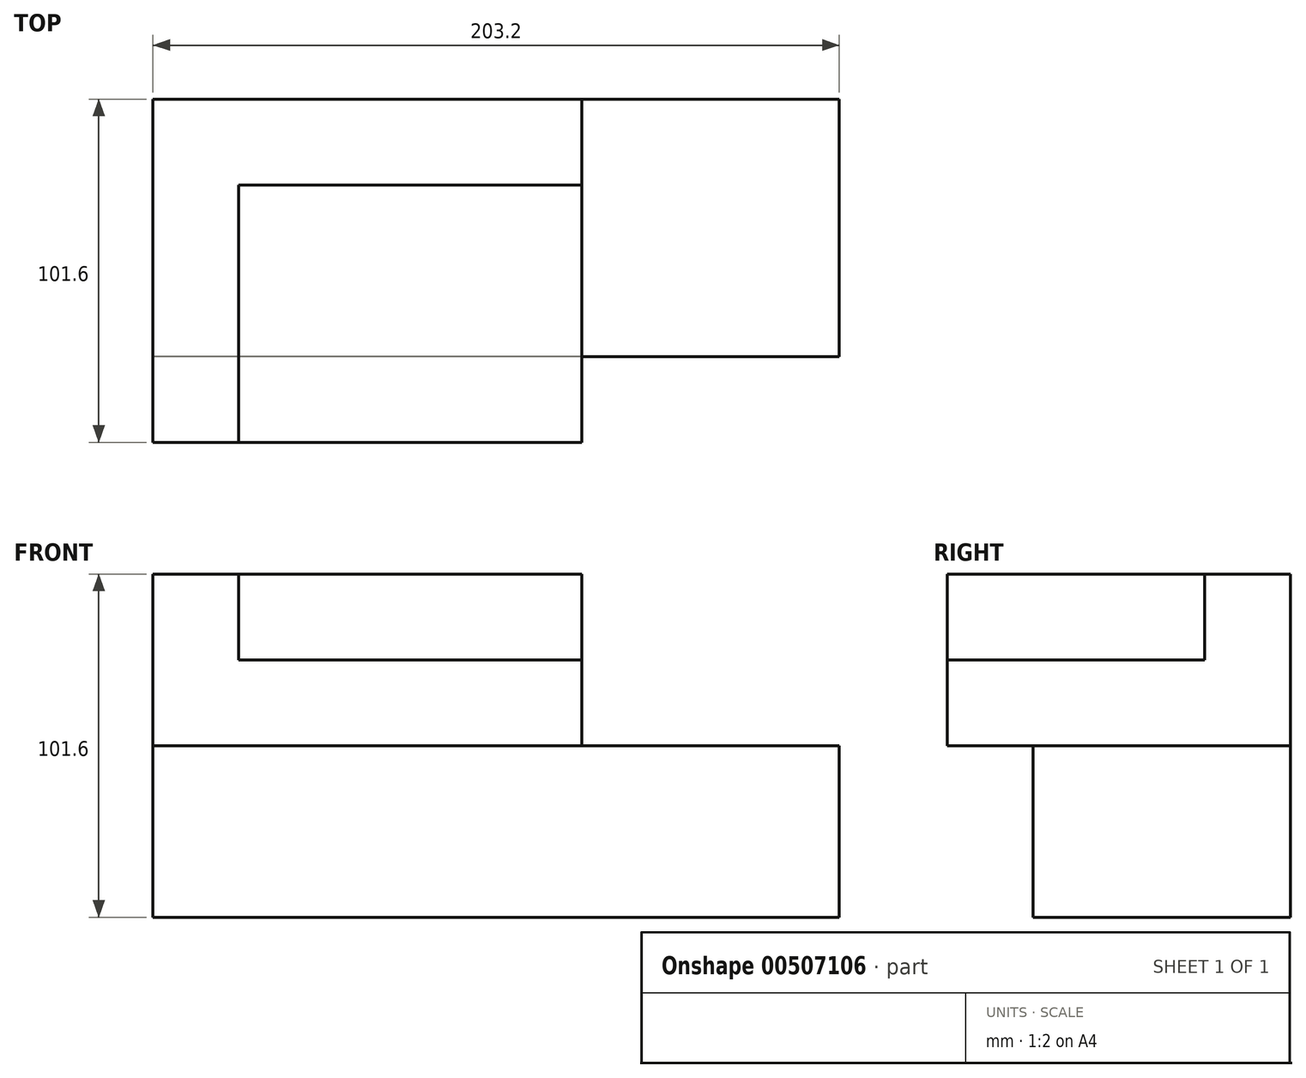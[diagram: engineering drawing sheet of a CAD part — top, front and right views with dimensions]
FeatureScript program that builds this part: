
annotation { "Feature Type Name" : "Feature", "Feature Type Description" : "" }
export const myFeature = defineFeature(function(context is Context, id is Id, definition is map)
    precondition{}
    {
        {
            var Q0;
            Q0=qCreatedBy(makeId("Top.planeOp"),FACE);
            var sketch = newSketch(context, id + "F0", { "sketchPlane" : qUnion([Q0])});
            skLineSegment(sketch, "E0", {"start": v(0, 0) * mm, "end": v(-203.2, 0) * mm});
            skLineSegment(sketch, "E1", {"start": v(-203.2, 0) * mm, "end": v(-203.2, 76.2) * mm});
            skLineSegment(sketch, "E2", {"start": v(-203.2, 76.2) * mm, "end": v(0, 76.2) * mm});
            skLineSegment(sketch, "E3", {"start": v(0, 76.2) * mm, "end": v(0, 0) * mm});
            skSolve(sketch);
        }
        {
            var Q0;
            Q0=makeQuery(id+"F0.imprint","IMPRINT",FACE,{"disambiguationData":[TD([[makeQuery(id+"F0.imprint","IMPRINT",EDGE,{"derivedFrom":sQuery(id+"F0.wireOp",EDGE,"E0")}),-1.0]])]});
            extrude(context, id + "F1", {"entities" : qUnion([Q0]), "depth" : 50.8 * mm});
        }
        {
            var Q0;
            Q0=makeQuery(id+"F1.opExtrude","CAP_FACE",FACE,{"disambiguationData":[OSD([sQuery(id+"F0.wireOp",EDGE,"E0"),sQuery(id+"F0.wireOp",EDGE,"E1"),sQuery(id+"F0.wireOp",EDGE,"E2"),sQuery(id+"F0.wireOp",EDGE,"E3")])],"isStart":false});
            var sketch = newSketch(context, id + "F2", { "sketchPlane" : qUnion([Q0])});
            skLineSegment(sketch, "E4", {"start": v(-203.2, 76.2) * mm, "end": v(-203.2, -25.4) * mm});
            skPoint(sketch, "E4.endSnap0", {"position": v(-203.2, 38.1) * mm});
            skLineSegment(sketch, "E5", {"start": v(-203.2, -25.4) * mm, "end": v(-76.2, -25.4) * mm});
            skLineSegment(sketch, "E6", {"start": v(-76.2, -25.4) * mm, "end": v(-76.2, 76.2) * mm});
            skLineSegment(sketch, "E7", {"start": v(-76.2, 76.2) * mm, "end": v(-203.2, 76.2) * mm});
            skSolve(sketch);
        }
        {
            var Q0;
            {var subQ3=sQuery(id+"F2.wireOp",EDGE,"E7");Q0=makeQuery(id+"F2.imprint","IMPRINT",FACE,{"disambiguationData":[TD([[makeQuery(id+"F2.imprint","IMPRINT",EDGE,{"derivedFrom":subQ3}),-1.0]])]});}
            var Q1;
            {var subQ3=sQuery(id+"F2.wireOp",EDGE,"E5");Q1=makeQuery(id+"F2.imprint","IMPRINT",FACE,{"disambiguationData":[TD([[makeQuery(id+"F2.imprint","IMPRINT",EDGE,{"derivedFrom":subQ3}),1.0]])]});}
            extrude(context, id + "F3", {"entities" : qUnion([Q0, Q1]), "operationType" : NewBodyOperationType.ADD, "depth" : 50.8 * mm});
        }
        {
            var Q0;
            Q0=makeQuery(id+"F3.opExtrude","CAP_FACE",FACE,{"disambiguationData":[OSD([sQuery(id+"F2.wireOp",EDGE,"E4"),sQuery(id+"F2.wireOp",EDGE,"E5"),sQuery(id+"F2.wireOp",EDGE,"E6"),sQuery(id+"F2.wireOp",EDGE,"E7")])],"isStart":false});
            var sketch = newSketch(context, id + "F4", { "sketchPlane" : qUnion([Q0])});
            skLineSegment(sketch, "E8", {"start": v(-76.2, -25.4) * mm, "end": v(-177.8, -25.4) * mm});
            skLineSegment(sketch, "E9", {"start": v(-177.8, -25.4) * mm, "end": v(-177.8, 50.8) * mm});
            skLineSegment(sketch, "E10", {"start": v(-177.8, 50.8) * mm, "end": v(-76.2, 50.8) * mm});
            skLineSegment(sketch, "E11", {"start": v(-76.2, 50.8) * mm, "end": v(-76.2, -25.4) * mm});
            skSolve(sketch);
        }
        {
            var Q0;
            Q0=makeQuery(id+"F4.imprint","IMPRINT",FACE,{"disambiguationData":[TD([[makeQuery(id+"F4.imprint","IMPRINT",EDGE,{"derivedFrom":sQuery(id+"F4.wireOp",EDGE,"E8")}),1.0]])]});
            extrude(context, id + "F5", {"entities" : qUnion([Q0]), "operationType" : NewBodyOperationType.REMOVE, "oppositeDirection" : true, "depth" : 25.4 * mm});
        }
    });
